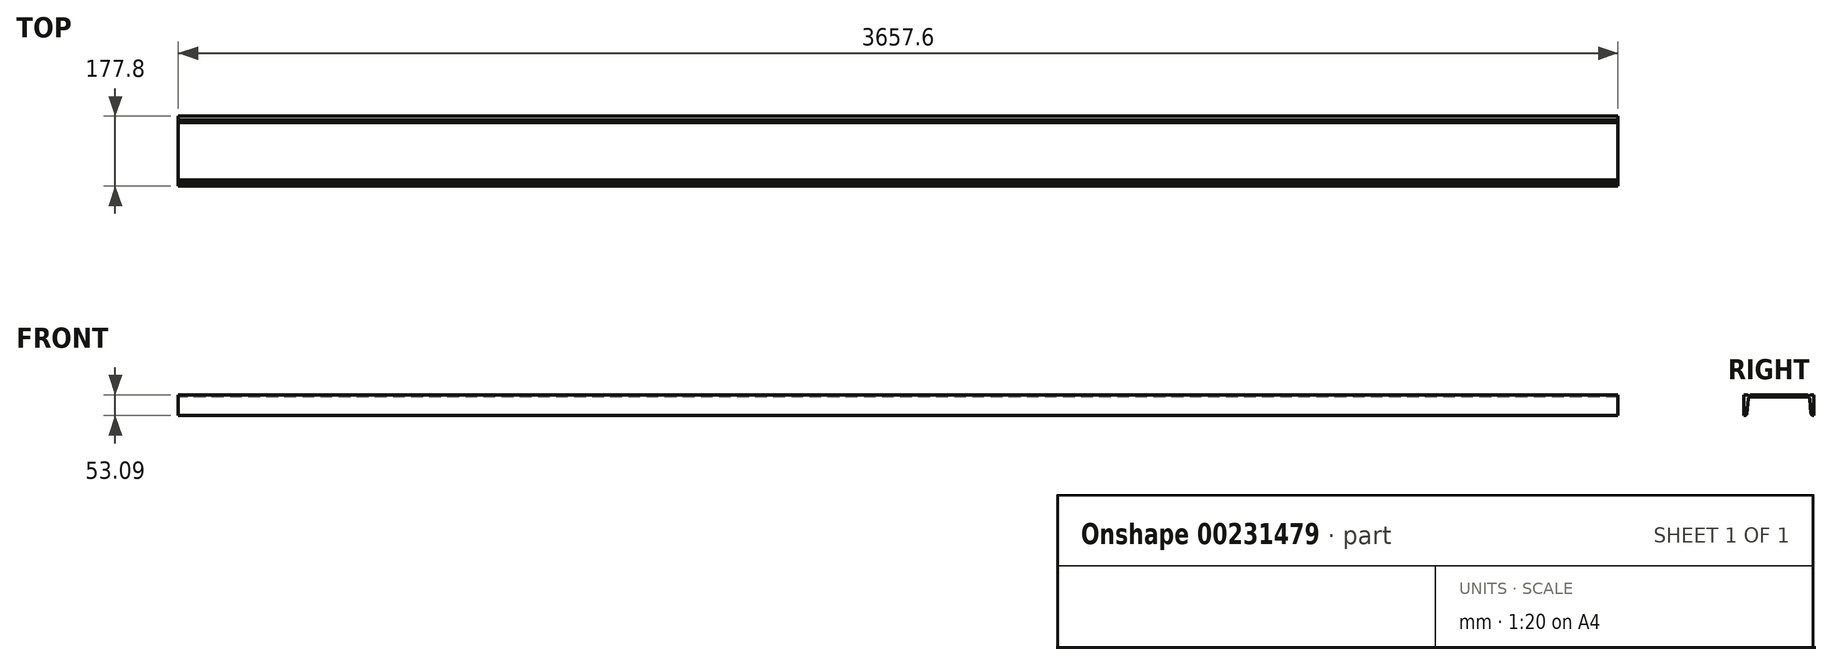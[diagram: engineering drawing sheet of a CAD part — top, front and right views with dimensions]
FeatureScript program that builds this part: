
annotation { "Feature Type Name" : "Feature", "Feature Type Description" : "" }
export const myFeature = defineFeature(function(context is Context, id is Id, definition is map)
    precondition{}
    {
        {
            var Q0;
            Q0=qCreatedBy(makeId("Right.planeOp"),FACE);
            var sketch = newSketch(context, id + "F0", { "sketchPlane" : qUnion([Q0])});
            skLineSegment(sketch, "E0", {"start": v(88.9, 0) * mm, "end": v(88.9, -53.09) * mm});
            skLineSegment(sketch, "E1", {"start": v(88.9, -53.09) * mm, "end": v(87.74, -53.09) * mm});
            skLineSegment(sketch, "E2", {"start": v(81.42, -47.29) * mm, "end": v(78.26, -11.13) * mm});
            skLineSegment(sketch, "E3", {"start": v(71.93, -5.33) * mm, "end": v(-71.93, -5.33) * mm});
            skLineSegment(sketch, "E4", {"start": v(-78.26, -11.13) * mm, "end": v(-81.42, -47.29) * mm});
            skLineSegment(sketch, "E5", {"start": v(-87.74, -53.09) * mm, "end": v(-88.9, -53.09) * mm});
            skLineSegment(sketch, "E6", {"start": v(-88.9, -53.09) * mm, "end": v(-88.9, 0) * mm});
            skLineSegment(sketch, "E7", {"start": v(-88.9, 0) * mm, "end": v(-79.38, 0) * mm});
            skLineSegment(sketch, "E8", {"start": v(-88.9, -26.54) * mm, "end": v(-79.6, -26.54) * mm, "construction": true});
            skLineSegment(sketch, "E9", {"start": v(88.9, -26.54) * mm, "end": v(79.6, -26.54) * mm});
            skPoint(sketch, "E10.visualSharp", {"position": v(-77.75, -5.33) * mm});
            skArc(sketch, "E10.filletArc", {"start": v(-71.93, -5.33) * mm, "mid": v(-76.22, -7) * mm, "end": v(-78.26, -11.13) * mm});
            skPoint(sketch, "E11.visualSharp", {"position": v(77.75, -5.33) * mm});
            skArc(sketch, "E11.filletArc", {"start": v(78.26, -11.13) * mm, "mid": v(76.22, -7) * mm, "end": v(71.93, -5.33) * mm});
            skPoint(sketch, "E12.visualSharp", {"position": v(81.93, -53.09) * mm});
            skArc(sketch, "E12.filletArc", {"start": v(81.42, -47.29) * mm, "mid": v(83.45, -51.42) * mm, "end": v(87.74, -53.09) * mm});
            skPoint(sketch, "E13.visualSharp", {"position": v(-81.93, -53.09) * mm});
            skArc(sketch, "E13.filletArc", {"start": v(-87.74, -53.09) * mm, "mid": v(-83.45, -51.42) * mm, "end": v(-81.42, -47.29) * mm});
            skLineSegment(sketch, "E14", {"start": v(-73.03, 0) * mm, "end": v(-76.2, -3.18) * mm});
            skLineSegment(sketch, "E15", {"start": v(-79.38, 0) * mm, "end": v(-76.2, -3.18) * mm});
            skLineSegment(sketch, "E16", {"start": v(73.03, 0) * mm, "end": v(76.2, -3.17) * mm});
            skLineSegment(sketch, "E17", {"start": v(76.2, -3.17) * mm, "end": v(79.38, 0) * mm});
            skLineSegment(sketch, "E18.trimOffspring", {"start": v(-73.03, 0) * mm, "end": v(73.03, 0) * mm});
            skLineSegment(sketch, "E19.trimOffspring", {"start": v(79.38, 0) * mm, "end": v(88.9, 0) * mm});
            skSolve(sketch);
        }
        {
            var Q0;
            Q0 = qSketchRegion(id + "F0", true);
            extrude(context, id + "F1", {"entities" : qUnion([Q0]), "depth" : 3657.6 * mm});
        }
    });
